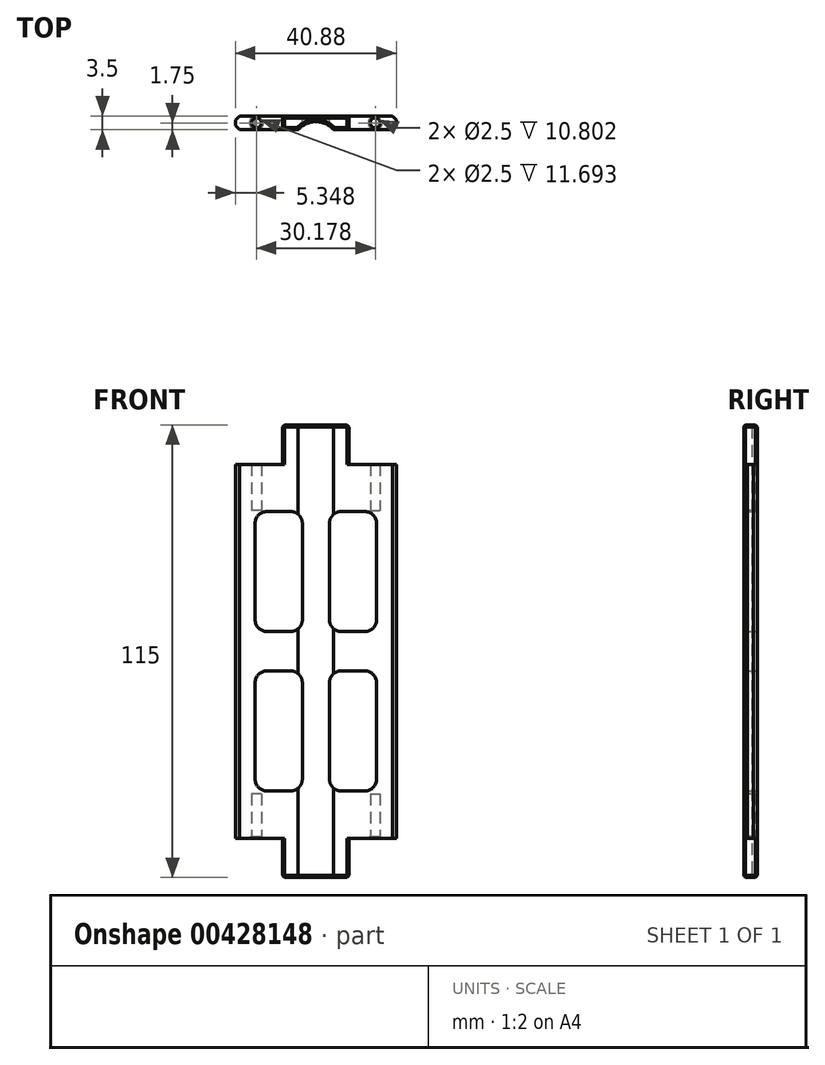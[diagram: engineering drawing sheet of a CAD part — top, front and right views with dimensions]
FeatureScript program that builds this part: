
annotation { "Feature Type Name" : "Feature", "Feature Type Description" : "" }
export const myFeature = defineFeature(function(context is Context, id is Id, definition is map)
    precondition{}
    {
        {
            var Q0;
            Q0=qCreatedBy(makeId("Top.planeOp"),FACE);
            var sketch = newSketch(context, id + "F0", { "sketchPlane" : qUnion([Q0])});
            skLineSegment(sketch, "E0", {"start": v(-26.48, 7.6) * mm, "end": v(-26.48, 21.4) * mm, "construction": true});
            skPoint(sketch, "E0.endSnap0", {"position": v(-26.48, 17.6) * mm});
            skLineSegment(sketch, "E1", {"start": v(-18.04, 15.1) * mm, "end": v(-18.04, 11.6) * mm});
            skLineSegment(sketch, "E2", {"start": v(-18.04, 11.6) * mm, "end": v(-21.94, 11.6) * mm});
            skLineSegment(sketch, "E3", {"start": v(-34.92, 11.6) * mm, "end": v(-34.92, 15.1) * mm});
            skLineSegment(sketch, "E4", {"start": v(-34.92, 15.1) * mm, "end": v(-18.04, 15.1) * mm});
            skArc(sketch, "E5", {"start": v(-21.94, 11.6) * mm, "mid": v(-26.48, 13.64) * mm, "end": v(-31.02, 11.6) * mm});
            skLineSegment(sketch, "E6.trimOffspring", {"start": v(-31.02, 11.6) * mm, "end": v(-34.92, 11.6) * mm});
            skLineSegment(sketch, "E7", {"start": v(-34.92, 13.34) * mm, "end": v(-1.9, 13.34) * mm, "construction": true});
            skLineSegment(sketch, "E8", {"start": v(-34.92, 13.34) * mm, "end": v(-48.22, 13.34) * mm, "construction": true});
            skCircle(sketch, "E9", {"center": v(-41.57, 13.34) * mm, "radius": 1.25 * mm});
            skCircle(sketch, "E10", {"center": v(-11.4, 13.34) * mm, "radius": 1.25 * mm});
            skSolve(sketch);
        }
        {
            var Q0;
            Q0=makeQuery(id+"F0.imprint","IMPRINT",FACE,{"disambiguationData":[TD([[makeQuery(id+"F0.imprint","IMPRINT",EDGE,{"derivedFrom":sQuery(id+"F0.wireOp",EDGE,"E1")}),-1.0]])]});
            extrude(context, id + "F1", {"entities" : qUnion([Q0]), "depth" : 115 * mm});
        }
        {
            var Q0;
            Q0=makeQuery(id+"F1.opExtrude","SWEPT_FACE",FACE,{"disambiguationData":[OSD([sQuery(id+"F0.wireOp",EDGE,"E1")])]});
            var sketch = newSketch(context, id + "F2", { "sketchPlane" : qUnion([Q0])});
            skLineSegment(sketch, "E11", {"start": v(11.6, 105) * mm, "end": v(15.1, 105) * mm});
            skLineSegment(sketch, "E12", {"start": v(15.1, 105) * mm, "end": v(15.1, 10) * mm});
            skLineSegment(sketch, "E13", {"start": v(15.1, 10) * mm, "end": v(11.6, 10) * mm});
            skLineSegment(sketch, "E14", {"start": v(11.6, 10) * mm, "end": v(11.6, 105) * mm});
            skSolve(sketch);
        }
        {
            var Q0;
            Q0=makeQuery(id+"F2.imprint","IMPRINT",FACE,{"disambiguationData":[TD([[makeQuery(id+"F2.imprint","IMPRINT",EDGE,{"derivedFrom":sQuery(id+"F2.wireOp",EDGE,"E11")}),-1.0]])]});
            extrude(context, id + "F3", {"entities" : qUnion([Q0]), "operationType" : NewBodyOperationType.ADD, "depth" : 12 * mm});
        }
        {
            var Q0;
            Q0=makeQuery(id+"F1.opExtrude","SWEPT_FACE",FACE,{"disambiguationData":[OSD([sQuery(id+"F0.wireOp",EDGE,"E3")])]});
            var sketch = newSketch(context, id + "F4", { "sketchPlane" : qUnion([Q0])});
            skLineSegment(sketch, "E15", {"start": v(-15.1, 105) * mm, "end": v(-11.6, 105) * mm});
            skLineSegment(sketch, "E16", {"start": v(-11.6, 105) * mm, "end": v(-11.6, 10) * mm});
            skLineSegment(sketch, "E17", {"start": v(-11.6, 10) * mm, "end": v(-15.1, 10) * mm});
            skLineSegment(sketch, "E18", {"start": v(-15.1, 10) * mm, "end": v(-15.1, 105) * mm});
            skSolve(sketch);
        }
        {
            var Q0;
            Q0=makeQuery(id+"F4.imprint","IMPRINT",FACE,{"disambiguationData":[TD([[makeQuery(id+"F4.imprint","IMPRINT",EDGE,{"derivedFrom":sQuery(id+"F4.wireOp",EDGE,"E15")}),-1.0]])]});
            extrude(context, id + "F5", {"entities" : qUnion([Q0]), "operationType" : NewBodyOperationType.ADD, "depth" : 12 * mm});
        }
        {
            var Q0;
            Q0=makeQuery(id+"F0.imprint","IMPRINT",FACE,{"disambiguationData":[TD([[makeQuery(id+"F0.imprint","IMPRINT",EDGE,{"derivedFrom":sQuery(id+"F0.wireOp",EDGE,"E9")}),1.0]])]});
            var Q1;
            Q1=makeQuery(id+"F0.imprint","IMPRINT",FACE,{"disambiguationData":[TD([[makeQuery(id+"F0.imprint","IMPRINT",EDGE,{"derivedFrom":sQuery(id+"F0.wireOp",EDGE,"E10")}),1.0]])]});
            var Q2;
            Q2=makeQuery(id+"F5.opExtrude","SWEPT_FACE",FACE,{"disambiguationData":[OSD([sQuery(id+"F4.wireOp",EDGE,"E15")])]});
            extrude(context, id + "F6", {"entities" : qUnion([Q0, Q1]), "operationType" : NewBodyOperationType.REMOVE, "endBound" : BoundingType.UP_TO_SURFACE, "endBoundEntityFace" : qUnion([Q2]), "depth" : 25 * mm});
        }
        {
            var Q0;
            Q0=makeQuery(id+"F5.boolean.opBoolean","MERGE",FACE,{"derivedFrom":[makeQuery(id+"F3.boolean.opBoolean","MERGE",FACE,{"derivedFrom":[makeQuery(id+"F1.opExtrude","SWEPT_FACE",FACE,{"disambiguationData":[OSD([sQuery(id+"F0.wireOp",EDGE,"E4")])]}),makeQuery(id+"F3.opExtrude","SWEPT_FACE",FACE,{"disambiguationData":[OSD([sQuery(id+"F2.wireOp",EDGE,"E12")])]})]}),makeQuery(id+"F5.opExtrude","SWEPT_FACE",FACE,{"disambiguationData":[OSD([sQuery(id+"F4.wireOp",EDGE,"E18")])]})]});
            var sketch = newSketch(context, id + "F7", { "sketchPlane" : qUnion([Q0])});
            skLineSegment(sketch, "E19.bottom", {"start": v(32.92, 93) * mm, "end": v(38.92, 93) * mm});
            skLineSegment(sketch, "E19.top", {"start": v(32.92, 62.5) * mm, "end": v(38.92, 62.5) * mm});
            skLineSegment(sketch, "E19.left", {"start": v(29.92, 90) * mm, "end": v(29.92, 65.5) * mm});
            skLineSegment(sketch, "E19.right", {"start": v(41.92, 90) * mm, "end": v(41.92, 65.5) * mm});
            skLineSegment(sketch, "E20", {"start": v(6.04, 105) * mm, "end": v(46.92, 105) * mm, "construction": true});
            skLineSegment(sketch, "E21", {"start": v(46.92, 105) * mm, "end": v(46.92, 10) * mm, "construction": true});
            skLineSegment(sketch, "E22", {"start": v(6.04, 57.5) * mm, "end": v(106.1, 57.5) * mm, "construction": true});
            skLineSegment(sketch, "E23", {"start": v(26.48, 105) * mm, "end": v(26.48, -23.84) * mm, "construction": true});
            skLineSegment(sketch, "E24.MirrorCS", {"start": v(20.04, 62.5) * mm, "end": v(14.04, 62.5) * mm});
            skLineSegment(sketch, "E25.MirrorCS", {"start": v(11.04, 90) * mm, "end": v(11.04, 65.5) * mm});
            skLineSegment(sketch, "E26.MirrorCS", {"start": v(20.04, 93) * mm, "end": v(14.04, 93) * mm});
            skLineSegment(sketch, "E27.MirrorCS", {"start": v(23.04, 90) * mm, "end": v(23.04, 65.5) * mm});
            skLineSegment(sketch, "E28.MirrorCS", {"start": v(20.04, 22) * mm, "end": v(14.04, 22) * mm});
            skLineSegment(sketch, "E29.MirrorCS", {"start": v(11.04, 25) * mm, "end": v(11.04, 49.5) * mm});
            skLineSegment(sketch, "E30.MirrorCS", {"start": v(20.04, 52.5) * mm, "end": v(14.04, 52.5) * mm});
            skLineSegment(sketch, "E31.MirrorCS", {"start": v(32.92, 52.5) * mm, "end": v(38.92, 52.5) * mm});
            skLineSegment(sketch, "E32.MirrorCS", {"start": v(32.92, 22) * mm, "end": v(38.92, 22) * mm});
            skLineSegment(sketch, "E33.MirrorCS", {"start": v(41.92, 25) * mm, "end": v(41.92, 49.5) * mm});
            skLineSegment(sketch, "E34.MirrorCS", {"start": v(29.92, 25) * mm, "end": v(29.92, 49.5) * mm});
            skLineSegment(sketch, "E35.MirrorCS", {"start": v(23.04, 25) * mm, "end": v(23.04, 49.5) * mm});
            skPoint(sketch, "E36.visualSharp", {"position": v(11.04, 93) * mm});
            skArc(sketch, "E36.filletArc", {"start": v(14.04, 93) * mm, "mid": v(11.92, 92.12) * mm, "end": v(11.04, 90) * mm});
            skPoint(sketch, "E37.visualSharp", {"position": v(23.04, 93) * mm});
            skArc(sketch, "E37.filletArc", {"start": v(23.04, 90) * mm, "mid": v(22.17, 92.12) * mm, "end": v(20.04, 93) * mm});
            skPoint(sketch, "E38.visualSharp", {"position": v(23.04, 62.5) * mm});
            skArc(sketch, "E38.filletArc", {"start": v(20.04, 62.5) * mm, "mid": v(22.17, 63.38) * mm, "end": v(23.04, 65.5) * mm});
            skPoint(sketch, "E39.visualSharp", {"position": v(11.04, 62.5) * mm});
            skArc(sketch, "E39.filletArc", {"start": v(11.04, 65.5) * mm, "mid": v(11.92, 63.38) * mm, "end": v(14.04, 62.5) * mm});
            skPoint(sketch, "E40.visualSharp", {"position": v(29.92, 93) * mm});
            skArc(sketch, "E40.filletArc", {"start": v(32.92, 93) * mm, "mid": v(30.8, 92.12) * mm, "end": v(29.92, 90) * mm});
            skPoint(sketch, "E41.visualSharp", {"position": v(41.92, 93) * mm});
            skArc(sketch, "E41.filletArc", {"start": v(41.92, 90) * mm, "mid": v(41.04, 92.12) * mm, "end": v(38.92, 93) * mm});
            skPoint(sketch, "E42.visualSharp", {"position": v(41.92, 62.5) * mm});
            skArc(sketch, "E42.filletArc", {"start": v(38.92, 62.5) * mm, "mid": v(41.04, 63.38) * mm, "end": v(41.92, 65.5) * mm});
            skPoint(sketch, "E43.visualSharp", {"position": v(29.92, 62.5) * mm});
            skArc(sketch, "E43.filletArc", {"start": v(29.92, 65.5) * mm, "mid": v(30.8, 63.38) * mm, "end": v(32.92, 62.5) * mm});
            skPoint(sketch, "E44.visualSharp", {"position": v(29.92, 52.5) * mm});
            skArc(sketch, "E44.filletArc", {"start": v(32.92, 52.5) * mm, "mid": v(30.8, 51.62) * mm, "end": v(29.92, 49.5) * mm});
            skPoint(sketch, "E45.visualSharp", {"position": v(41.92, 52.5) * mm});
            skArc(sketch, "E45.filletArc", {"start": v(41.92, 49.5) * mm, "mid": v(41.04, 51.62) * mm, "end": v(38.92, 52.5) * mm});
            skPoint(sketch, "E46.visualSharp", {"position": v(41.92, 22) * mm});
            skArc(sketch, "E46.filletArc", {"start": v(38.92, 22) * mm, "mid": v(41.04, 22.88) * mm, "end": v(41.92, 25) * mm});
            skPoint(sketch, "E47.visualSharp", {"position": v(29.92, 22) * mm});
            skArc(sketch, "E47.filletArc", {"start": v(29.92, 25) * mm, "mid": v(30.8, 22.88) * mm, "end": v(32.92, 22) * mm});
            skPoint(sketch, "E48.visualSharp", {"position": v(23.04, 52.5) * mm});
            skArc(sketch, "E48.filletArc", {"start": v(23.04, 49.5) * mm, "mid": v(22.17, 51.62) * mm, "end": v(20.04, 52.5) * mm});
            skPoint(sketch, "E49.visualSharp", {"position": v(11.04, 52.5) * mm});
            skArc(sketch, "E49.filletArc", {"start": v(14.04, 52.5) * mm, "mid": v(11.92, 51.62) * mm, "end": v(11.04, 49.5) * mm});
            skPoint(sketch, "E50.visualSharp", {"position": v(11.04, 22) * mm});
            skArc(sketch, "E50.filletArc", {"start": v(11.04, 25) * mm, "mid": v(11.92, 22.88) * mm, "end": v(14.04, 22) * mm});
            skPoint(sketch, "E51.visualSharp", {"position": v(23.04, 22) * mm});
            skArc(sketch, "E51.filletArc", {"start": v(20.04, 22) * mm, "mid": v(22.17, 22.88) * mm, "end": v(23.04, 25) * mm});
            skSolve(sketch);
        }
        {
            var Q0;
            Q0=makeQuery(id+"F7.imprint","IMPRINT",FACE,{"disambiguationData":[TD([[makeQuery(id+"F7.imprint","IMPRINT",EDGE,{"derivedFrom":sQuery(id+"F7.wireOp",EDGE,"E24.MirrorCS")}),-1.0]])]});
            var Q1;
            Q1=makeQuery(id+"F7.imprint","IMPRINT",FACE,{"disambiguationData":[TD([[makeQuery(id+"F7.imprint","IMPRINT",EDGE,{"derivedFrom":sQuery(id+"F7.wireOp",EDGE,"E19.bottom")}),-1.0]])]});
            var Q2;
            Q2=makeQuery(id+"F7.imprint","IMPRINT",FACE,{"disambiguationData":[TD([[makeQuery(id+"F7.imprint","IMPRINT",EDGE,{"derivedFrom":sQuery(id+"F7.wireOp",EDGE,"E28.MirrorCS")}),-1.0]])]});
            var Q3;
            Q3=makeQuery(id+"F7.imprint","IMPRINT",FACE,{"disambiguationData":[TD([[makeQuery(id+"F7.imprint","IMPRINT",EDGE,{"derivedFrom":sQuery(id+"F7.wireOp",EDGE,"E31.MirrorCS")}),-1.0]])]});
            var Q4;
            Q4=makeQuery(id+"F3.boolean.opBoolean","MERGE",FACE,{"derivedFrom":[makeQuery(id+"F1.opExtrude","SWEPT_FACE",FACE,{"disambiguationData":[OSD([sQuery(id+"F0.wireOp",EDGE,"E2")])]}),makeQuery(id+"F3.opExtrude","SWEPT_FACE",FACE,{"disambiguationData":[OSD([sQuery(id+"F2.wireOp",EDGE,"E14")])]})]});
            extrude(context, id + "F8", {"entities" : qUnion([Q0, Q1, Q2, Q3]), "operationType" : NewBodyOperationType.REMOVE, "endBound" : BoundingType.UP_TO_SURFACE, "oppositeDirection" : true, "endBoundEntityFace" : qUnion([Q4]), "depth" : 25 * mm});
        }
        {
            var Q0;
            Q0=makeQuery(id+"F5.boolean.opBoolean","MERGE",FACE,{"derivedFrom":[makeQuery(id+"F1.opExtrude","SWEPT_FACE",FACE,{"disambiguationData":[OSD([sQuery(id+"F0.wireOp",EDGE,"E6.trimOffspring")])]}),makeQuery(id+"F5.opExtrude","SWEPT_FACE",FACE,{"disambiguationData":[OSD([sQuery(id+"F4.wireOp",EDGE,"E16")])]})]});
            var sketch = newSketch(context, id + "F9", { "sketchPlane" : qUnion([Q0])});
            skLineSegment(sketch, "E52.bottom", {"start": v(-14.55, 93.3) * mm, "end": v(-8.57, 93.3) * mm});
            skLineSegment(sketch, "E52.top", {"start": v(-14.55, 21.3) * mm, "end": v(-8.57, 21.3) * mm});
            skLineSegment(sketch, "E52.right", {"start": v(-8.57, 93.3) * mm, "end": v(-8.57, 21.3) * mm});
            skLineSegment(sketch, "E53", {"start": v(-14.55, 93.3) * mm, "end": v(-14.55, 93) * mm});
            skLineSegment(sketch, "E54", {"start": v(-34.92, 115) * mm, "end": v(-17.69, 115) * mm, "construction": true});
            skLineSegment(sketch, "E55", {"start": v(-26.3, 115) * mm, "end": v(-26.3, -16.22) * mm, "construction": true});
            skLineSegment(sketch, "E56.MirrorCS", {"start": v(-38.06, 93.3) * mm, "end": v(-38.06, 21.3) * mm});
            skLineSegment(sketch, "E57.MirrorCS", {"start": v(-38.06, 21.3) * mm, "end": v(-44.05, 21.3) * mm});
            skLineSegment(sketch, "E58.MirrorCS", {"start": v(-44.05, 93.3) * mm, "end": v(-44.05, 21.3) * mm});
            skLineSegment(sketch, "E59.MirrorCS", {"start": v(-38.06, 93.3) * mm, "end": v(-44.05, 93.3) * mm});
            skLineSegment(sketch, "E60.0", {"start": v(-11.04, 90) * mm, "end": v(-11.04, 65.5) * mm});
            skArc(sketch, "E60.1", {"start": v(-14.04, 93) * mm, "mid": v(-11.92, 92.12) * mm, "end": v(-11.04, 90) * mm});
            skArc(sketch, "E60.2", {"start": v(-11.04, 65.5) * mm, "mid": v(-11.92, 63.38) * mm, "end": v(-14.04, 62.5) * mm});
            skLineSegment(sketch, "E60.3", {"start": v(-14.55, 62.5) * mm, "end": v(-14.04, 62.5) * mm});
            skLineSegment(sketch, "E60.4", {"start": v(-14.55, 93) * mm, "end": v(-14.04, 93) * mm});
            skPoint(sketch, "E61.orphan", {"position": v(-20.04, 93) * mm});
            skLineSegment(sketch, "E62.trimOffspring", {"start": v(-14.55, 62.5) * mm, "end": v(-14.55, 52.5) * mm});
            skPoint(sketch, "E63.orphan", {"position": v(-20.04, 62.5) * mm});
            skLineSegment(sketch, "E64.0", {"start": v(-14.55, 52.5) * mm, "end": v(-14.04, 52.5) * mm});
            skArc(sketch, "E64.1", {"start": v(-14.04, 52.5) * mm, "mid": v(-11.92, 51.62) * mm, "end": v(-11.04, 49.5) * mm});
            skLineSegment(sketch, "E64.2", {"start": v(-11.04, 25) * mm, "end": v(-11.04, 49.5) * mm});
            skLineSegment(sketch, "E64.3", {"start": v(-14.55, 22) * mm, "end": v(-14.04, 22) * mm});
            skArc(sketch, "E64.4", {"start": v(-11.04, 25) * mm, "mid": v(-11.92, 22.88) * mm, "end": v(-14.04, 22) * mm});
            skPoint(sketch, "E64.5", {"position": v(-11.04, 37.25) * mm});
            skPoint(sketch, "E65.orphan", {"position": v(-20.04, 52.5) * mm});
            skPoint(sketch, "E66.orphan", {"position": v(-20.04, 22) * mm});
            skLineSegment(sketch, "E67.trimOffspring", {"start": v(-14.55, 22) * mm, "end": v(-14.55, 21.3) * mm});
            skSolve(sketch);
        }
        {
            var Q0;
            {var subQ4=sQuery(id+"F9.wireOp",EDGE,"E57.MirrorCS");Q0=makeQuery(id+"F9.imprint","IMPRINT",FACE,{"disambiguationData":[TD([[makeQuery(id+"F9.imprint","IMPRINT",EDGE,{"derivedFrom":subQ4}),-1.0]])]});}
            var Q1;
            Q1=makeQuery(id+"F9.imprint","IMPRINT",FACE,{"disambiguationData":[TD([[makeQuery(id+"F9.imprint","IMPRINT",EDGE,{"derivedFrom":sQuery(id+"F9.wireOp",EDGE,"E52.bottom")}),-1.0]])]});
            var Q2;
            Q2=makeQuery(id+"F5.boolean.opBoolean","MERGE",FACE,{"derivedFrom":[makeQuery(id+"F3.boolean.opBoolean","MERGE",FACE,{"derivedFrom":[makeQuery(id+"F1.opExtrude","SWEPT_FACE",FACE,{"disambiguationData":[OSD([sQuery(id+"F0.wireOp",EDGE,"E4")])]}),makeQuery(id+"F3.opExtrude","SWEPT_FACE",FACE,{"disambiguationData":[OSD([sQuery(id+"F2.wireOp",EDGE,"E12")])]})]}),makeQuery(id+"F5.opExtrude","SWEPT_FACE",FACE,{"disambiguationData":[OSD([sQuery(id+"F4.wireOp",EDGE,"E18")])]})]});
            extrude(context, id + "F10", {"entities" : qUnion([Q0, Q1]), "operationType" : NewBodyOperationType.ADD, "endBound" : BoundingType.UP_TO_SURFACE, "oppositeDirection" : true, "endBoundEntityFace" : qUnion([Q2]), "depth" : 25 * mm});
        }
        {
            var Q0;
            Q0=makeQuery(id+"F8.boolean.opBoolean","COPY",EDGE,{"derivedFrom":makeQuery(id+"F8.opExtrude","TWEAK_EDGE",EDGE,{"derivedFrom":[makeQuery(id+"F3.boolean.opBoolean","MERGE",FACE,{"derivedFrom":[makeQuery(id+"F1.opExtrude","SWEPT_FACE",FACE,{"disambiguationData":[OSD([sQuery(id+"F0.wireOp",EDGE,"E2")])]}),makeQuery(id+"F3.opExtrude","SWEPT_FACE",FACE,{"disambiguationData":[OSD([sQuery(id+"F2.wireOp",EDGE,"E14")])]})]}),makeQuery(id+"F7.imprint","IMPRINT",EDGE,{"derivedFrom":sQuery(id+"F7.wireOp",EDGE,"E33.MirrorCS")})]})});
            var Q1;
            Q1=makeQuery(id+"F8.boolean.opBoolean","COPY",EDGE,{"derivedFrom":makeQuery(id+"F8.opExtrude","TWEAK_EDGE",EDGE,{"derivedFrom":[makeQuery(id+"F3.boolean.opBoolean","MERGE",FACE,{"derivedFrom":[makeQuery(id+"F1.opExtrude","SWEPT_FACE",FACE,{"disambiguationData":[OSD([sQuery(id+"F0.wireOp",EDGE,"E2")])]}),makeQuery(id+"F3.opExtrude","SWEPT_FACE",FACE,{"disambiguationData":[OSD([sQuery(id+"F2.wireOp",EDGE,"E14")])]})]}),makeQuery(id+"F7.imprint","IMPRINT",EDGE,{"derivedFrom":sQuery(id+"F7.wireOp",EDGE,"E45.filletArc")})]})});
            var Q2;
            Q2=makeQuery(id+"F8.boolean.opBoolean","COPY",EDGE,{"derivedFrom":makeQuery(id+"F8.opExtrude","TWEAK_EDGE",EDGE,{"derivedFrom":[makeQuery(id+"F3.boolean.opBoolean","MERGE",FACE,{"derivedFrom":[makeQuery(id+"F1.opExtrude","SWEPT_FACE",FACE,{"disambiguationData":[OSD([sQuery(id+"F0.wireOp",EDGE,"E2")])]}),makeQuery(id+"F3.opExtrude","SWEPT_FACE",FACE,{"disambiguationData":[OSD([sQuery(id+"F2.wireOp",EDGE,"E14")])]})]}),makeQuery(id+"F7.imprint","IMPRINT",EDGE,{"derivedFrom":sQuery(id+"F7.wireOp",EDGE,"E31.MirrorCS")})]})});
            var Q3;
            Q3=makeQuery(id+"F8.boolean.opBoolean","COPY",EDGE,{"derivedFrom":makeQuery(id+"F8.opExtrude","TWEAK_EDGE",EDGE,{"derivedFrom":[makeQuery(id+"F3.boolean.opBoolean","MERGE",FACE,{"derivedFrom":[makeQuery(id+"F1.opExtrude","SWEPT_FACE",FACE,{"disambiguationData":[OSD([sQuery(id+"F0.wireOp",EDGE,"E2")])]}),makeQuery(id+"F3.opExtrude","SWEPT_FACE",FACE,{"disambiguationData":[OSD([sQuery(id+"F2.wireOp",EDGE,"E14")])]})]}),makeQuery(id+"F7.imprint","IMPRINT",EDGE,{"derivedFrom":sQuery(id+"F7.wireOp",EDGE,"E44.filletArc")})]})});
            var Q4;
            Q4=makeQuery(id+"F8.boolean.opBoolean","COPY",EDGE,{"derivedFrom":makeQuery(id+"F8.opExtrude","TWEAK_EDGE",EDGE,{"derivedFrom":[makeQuery(id+"F3.boolean.opBoolean","MERGE",FACE,{"derivedFrom":[makeQuery(id+"F1.opExtrude","SWEPT_FACE",FACE,{"disambiguationData":[OSD([sQuery(id+"F0.wireOp",EDGE,"E2")])]}),makeQuery(id+"F3.opExtrude","SWEPT_FACE",FACE,{"disambiguationData":[OSD([sQuery(id+"F2.wireOp",EDGE,"E14")])]})]}),makeQuery(id+"F7.imprint","IMPRINT",EDGE,{"derivedFrom":sQuery(id+"F7.wireOp",EDGE,"E47.filletArc")})]})});
            var Q5;
            Q5=makeQuery(id+"F8.boolean.opBoolean","COPY",EDGE,{"derivedFrom":makeQuery(id+"F8.opExtrude","TWEAK_EDGE",EDGE,{"derivedFrom":[makeQuery(id+"F3.boolean.opBoolean","MERGE",FACE,{"derivedFrom":[makeQuery(id+"F1.opExtrude","SWEPT_FACE",FACE,{"disambiguationData":[OSD([sQuery(id+"F0.wireOp",EDGE,"E2")])]}),makeQuery(id+"F3.opExtrude","SWEPT_FACE",FACE,{"disambiguationData":[OSD([sQuery(id+"F2.wireOp",EDGE,"E14")])]})]}),makeQuery(id+"F7.imprint","IMPRINT",EDGE,{"derivedFrom":sQuery(id+"F7.wireOp",EDGE,"E32.MirrorCS")})]})});
            var Q6;
            Q6=makeQuery(id+"F8.boolean.opBoolean","COPY",EDGE,{"derivedFrom":makeQuery(id+"F8.opExtrude","TWEAK_EDGE",EDGE,{"derivedFrom":[makeQuery(id+"F3.boolean.opBoolean","MERGE",FACE,{"derivedFrom":[makeQuery(id+"F1.opExtrude","SWEPT_FACE",FACE,{"disambiguationData":[OSD([sQuery(id+"F0.wireOp",EDGE,"E2")])]}),makeQuery(id+"F3.opExtrude","SWEPT_FACE",FACE,{"disambiguationData":[OSD([sQuery(id+"F2.wireOp",EDGE,"E14")])]})]}),makeQuery(id+"F7.imprint","IMPRINT",EDGE,{"derivedFrom":sQuery(id+"F7.wireOp",EDGE,"E46.filletArc")})]})});
            var Q7;
            Q7=makeQuery(id+"F8.boolean.opBoolean","COPY",EDGE,{"derivedFrom":makeQuery(id+"F8.opExtrude","CAP_EDGE",EDGE,{"disambiguationData":[OSD([sQuery(id+"F7.wireOp",EDGE,"E33.MirrorCS")])],"isStart":true})});
            var Q8;
            Q8=makeQuery(id+"F8.boolean.opBoolean","COPY",EDGE,{"derivedFrom":makeQuery(id+"F8.opExtrude","CAP_EDGE",EDGE,{"disambiguationData":[OSD([sQuery(id+"F7.wireOp",EDGE,"E45.filletArc")])],"isStart":true})});
            var Q9;
            Q9=makeQuery(id+"F8.boolean.opBoolean","COPY",EDGE,{"derivedFrom":makeQuery(id+"F8.opExtrude","CAP_EDGE",EDGE,{"disambiguationData":[OSD([sQuery(id+"F7.wireOp",EDGE,"E31.MirrorCS")])],"isStart":true})});
            var Q10;
            Q10=makeQuery(id+"F8.boolean.opBoolean","COPY",EDGE,{"derivedFrom":makeQuery(id+"F8.opExtrude","CAP_EDGE",EDGE,{"disambiguationData":[OSD([sQuery(id+"F7.wireOp",EDGE,"E44.filletArc")])],"isStart":true})});
            var Q11;
            Q11=makeQuery(id+"F8.boolean.opBoolean","COPY",EDGE,{"derivedFrom":makeQuery(id+"F8.opExtrude","TWEAK_EDGE",EDGE,{"derivedFrom":[makeQuery(id+"F3.boolean.opBoolean","MERGE",FACE,{"derivedFrom":[makeQuery(id+"F1.opExtrude","SWEPT_FACE",FACE,{"disambiguationData":[OSD([sQuery(id+"F0.wireOp",EDGE,"E2")])]}),makeQuery(id+"F3.opExtrude","SWEPT_FACE",FACE,{"disambiguationData":[OSD([sQuery(id+"F2.wireOp",EDGE,"E14")])]})]}),makeQuery(id+"F7.imprint","IMPRINT",EDGE,{"derivedFrom":sQuery(id+"F7.wireOp",EDGE,"E30.MirrorCS")})]})});
            var Q12;
            Q12=makeQuery(id+"F8.boolean.opBoolean","COPY",EDGE,{"derivedFrom":makeQuery(id+"F8.opExtrude","TWEAK_EDGE",EDGE,{"derivedFrom":[makeQuery(id+"F3.boolean.opBoolean","MERGE",FACE,{"derivedFrom":[makeQuery(id+"F1.opExtrude","SWEPT_FACE",FACE,{"disambiguationData":[OSD([sQuery(id+"F0.wireOp",EDGE,"E2")])]}),makeQuery(id+"F3.opExtrude","SWEPT_FACE",FACE,{"disambiguationData":[OSD([sQuery(id+"F2.wireOp",EDGE,"E14")])]})]}),makeQuery(id+"F7.imprint","IMPRINT",EDGE,{"derivedFrom":sQuery(id+"F7.wireOp",EDGE,"E48.filletArc")})]})});
            var Q13;
            Q13=makeQuery(id+"F8.boolean.opBoolean","COPY",EDGE,{"derivedFrom":makeQuery(id+"F8.opExtrude","TWEAK_EDGE",EDGE,{"derivedFrom":[makeQuery(id+"F3.boolean.opBoolean","MERGE",FACE,{"derivedFrom":[makeQuery(id+"F1.opExtrude","SWEPT_FACE",FACE,{"disambiguationData":[OSD([sQuery(id+"F0.wireOp",EDGE,"E2")])]}),makeQuery(id+"F3.opExtrude","SWEPT_FACE",FACE,{"disambiguationData":[OSD([sQuery(id+"F2.wireOp",EDGE,"E14")])]})]}),makeQuery(id+"F7.imprint","IMPRINT",EDGE,{"derivedFrom":sQuery(id+"F7.wireOp",EDGE,"E51.filletArc")})]})});
            var Q14;
            Q14=makeQuery(id+"F8.boolean.opBoolean","COPY",EDGE,{"derivedFrom":makeQuery(id+"F8.opExtrude","TWEAK_EDGE",EDGE,{"derivedFrom":[makeQuery(id+"F3.boolean.opBoolean","MERGE",FACE,{"derivedFrom":[makeQuery(id+"F1.opExtrude","SWEPT_FACE",FACE,{"disambiguationData":[OSD([sQuery(id+"F0.wireOp",EDGE,"E2")])]}),makeQuery(id+"F3.opExtrude","SWEPT_FACE",FACE,{"disambiguationData":[OSD([sQuery(id+"F2.wireOp",EDGE,"E14")])]})]}),makeQuery(id+"F7.imprint","IMPRINT",EDGE,{"derivedFrom":sQuery(id+"F7.wireOp",EDGE,"E28.MirrorCS")})]})});
            var Q15;
            Q15=makeQuery(id+"F8.boolean.opBoolean","COPY",EDGE,{"derivedFrom":makeQuery(id+"F8.opExtrude","TWEAK_EDGE",EDGE,{"derivedFrom":[makeQuery(id+"F3.boolean.opBoolean","MERGE",FACE,{"derivedFrom":[makeQuery(id+"F1.opExtrude","SWEPT_FACE",FACE,{"disambiguationData":[OSD([sQuery(id+"F0.wireOp",EDGE,"E2")])]}),makeQuery(id+"F3.opExtrude","SWEPT_FACE",FACE,{"disambiguationData":[OSD([sQuery(id+"F2.wireOp",EDGE,"E14")])]})]}),makeQuery(id+"F7.imprint","IMPRINT",EDGE,{"derivedFrom":sQuery(id+"F7.wireOp",EDGE,"E50.filletArc")})]})});
            var Q16;
            Q16=makeQuery(id+"F8.boolean.opBoolean","COPY",EDGE,{"derivedFrom":makeQuery(id+"F8.opExtrude","TWEAK_EDGE",EDGE,{"derivedFrom":[makeQuery(id+"F3.boolean.opBoolean","MERGE",FACE,{"derivedFrom":[makeQuery(id+"F1.opExtrude","SWEPT_FACE",FACE,{"disambiguationData":[OSD([sQuery(id+"F0.wireOp",EDGE,"E2")])]}),makeQuery(id+"F3.opExtrude","SWEPT_FACE",FACE,{"disambiguationData":[OSD([sQuery(id+"F2.wireOp",EDGE,"E14")])]})]}),makeQuery(id+"F7.imprint","IMPRINT",EDGE,{"derivedFrom":sQuery(id+"F7.wireOp",EDGE,"E29.MirrorCS")})]})});
            var Q17;
            Q17=makeQuery(id+"F8.boolean.opBoolean","COPY",EDGE,{"derivedFrom":makeQuery(id+"F8.opExtrude","TWEAK_EDGE",EDGE,{"derivedFrom":[makeQuery(id+"F3.boolean.opBoolean","MERGE",FACE,{"derivedFrom":[makeQuery(id+"F1.opExtrude","SWEPT_FACE",FACE,{"disambiguationData":[OSD([sQuery(id+"F0.wireOp",EDGE,"E2")])]}),makeQuery(id+"F3.opExtrude","SWEPT_FACE",FACE,{"disambiguationData":[OSD([sQuery(id+"F2.wireOp",EDGE,"E14")])]})]}),makeQuery(id+"F7.imprint","IMPRINT",EDGE,{"derivedFrom":sQuery(id+"F7.wireOp",EDGE,"E49.filletArc")})]})});
            var Q18;
            Q18=makeQuery(id+"F8.boolean.opBoolean","COPY",EDGE,{"derivedFrom":makeQuery(id+"F8.opExtrude","CAP_EDGE",EDGE,{"disambiguationData":[OSD([sQuery(id+"F7.wireOp",EDGE,"E35.MirrorCS")])],"isStart":true})});
            var Q19;
            Q19=makeQuery(id+"F8.boolean.opBoolean","COPY",EDGE,{"derivedFrom":makeQuery(id+"F8.opExtrude","CAP_EDGE",EDGE,{"disambiguationData":[OSD([sQuery(id+"F7.wireOp",EDGE,"E48.filletArc")])],"isStart":true})});
            var Q20;
            Q20=makeQuery(id+"F8.boolean.opBoolean","COPY",EDGE,{"derivedFrom":makeQuery(id+"F8.opExtrude","CAP_EDGE",EDGE,{"disambiguationData":[OSD([sQuery(id+"F7.wireOp",EDGE,"E30.MirrorCS")])],"isStart":true})});
            var Q21;
            Q21=makeQuery(id+"F8.boolean.opBoolean","COPY",EDGE,{"derivedFrom":makeQuery(id+"F8.opExtrude","CAP_EDGE",EDGE,{"disambiguationData":[OSD([sQuery(id+"F7.wireOp",EDGE,"E46.filletArc")])],"isStart":true})});
            var Q22;
            Q22=makeQuery(id+"F8.boolean.opBoolean","COPY",EDGE,{"derivedFrom":makeQuery(id+"F8.opExtrude","CAP_EDGE",EDGE,{"disambiguationData":[OSD([sQuery(id+"F7.wireOp",EDGE,"E32.MirrorCS")])],"isStart":true})});
            var Q23;
            Q23=makeQuery(id+"F8.boolean.opBoolean","COPY",EDGE,{"derivedFrom":makeQuery(id+"F8.opExtrude","CAP_EDGE",EDGE,{"disambiguationData":[OSD([sQuery(id+"F7.wireOp",EDGE,"E47.filletArc")])],"isStart":true})});
            var Q24;
            Q24=makeQuery(id+"F8.boolean.opBoolean","COPY",EDGE,{"derivedFrom":makeQuery(id+"F8.opExtrude","CAP_EDGE",EDGE,{"disambiguationData":[OSD([sQuery(id+"F7.wireOp",EDGE,"E51.filletArc")])],"isStart":true})});
            var Q25;
            Q25=makeQuery(id+"F8.boolean.opBoolean","COPY",EDGE,{"derivedFrom":makeQuery(id+"F8.opExtrude","CAP_EDGE",EDGE,{"disambiguationData":[OSD([sQuery(id+"F7.wireOp",EDGE,"E28.MirrorCS")])],"isStart":true})});
            var Q26;
            Q26=makeQuery(id+"F8.boolean.opBoolean","COPY",EDGE,{"derivedFrom":makeQuery(id+"F8.opExtrude","CAP_EDGE",EDGE,{"disambiguationData":[OSD([sQuery(id+"F7.wireOp",EDGE,"E50.filletArc")])],"isStart":true})});
            var Q27;
            Q27=makeQuery(id+"F8.boolean.opBoolean","COPY",EDGE,{"derivedFrom":makeQuery(id+"F8.opExtrude","CAP_EDGE",EDGE,{"disambiguationData":[OSD([sQuery(id+"F7.wireOp",EDGE,"E29.MirrorCS")])],"isStart":true})});
            var Q28;
            Q28=makeQuery(id+"F8.boolean.opBoolean","COPY",EDGE,{"derivedFrom":makeQuery(id+"F8.opExtrude","CAP_EDGE",EDGE,{"disambiguationData":[OSD([sQuery(id+"F7.wireOp",EDGE,"E49.filletArc")])],"isStart":true})});
            var Q29;
            Q29=makeQuery(id+"F8.boolean.opBoolean","COPY",EDGE,{"derivedFrom":makeQuery(id+"F8.opExtrude","CAP_EDGE",EDGE,{"disambiguationData":[OSD([sQuery(id+"F7.wireOp",EDGE,"E43.filletArc")])],"isStart":true})});
            var Q30;
            Q30=makeQuery(id+"F8.boolean.opBoolean","COPY",EDGE,{"derivedFrom":makeQuery(id+"F8.opExtrude","TWEAK_EDGE",EDGE,{"derivedFrom":[makeQuery(id+"F3.boolean.opBoolean","MERGE",FACE,{"derivedFrom":[makeQuery(id+"F1.opExtrude","SWEPT_FACE",FACE,{"disambiguationData":[OSD([sQuery(id+"F0.wireOp",EDGE,"E2")])]}),makeQuery(id+"F3.opExtrude","SWEPT_FACE",FACE,{"disambiguationData":[OSD([sQuery(id+"F2.wireOp",EDGE,"E14")])]})]}),makeQuery(id+"F7.imprint","IMPRINT",EDGE,{"derivedFrom":sQuery(id+"F7.wireOp",EDGE,"E43.filletArc")})]})});
            var Q31;
            Q31=makeQuery(id+"F8.boolean.opBoolean","COPY",EDGE,{"derivedFrom":makeQuery(id+"F8.opExtrude","TWEAK_EDGE",EDGE,{"derivedFrom":[makeQuery(id+"F3.boolean.opBoolean","MERGE",FACE,{"derivedFrom":[makeQuery(id+"F1.opExtrude","SWEPT_FACE",FACE,{"disambiguationData":[OSD([sQuery(id+"F0.wireOp",EDGE,"E2")])]}),makeQuery(id+"F3.opExtrude","SWEPT_FACE",FACE,{"disambiguationData":[OSD([sQuery(id+"F2.wireOp",EDGE,"E14")])]})]}),makeQuery(id+"F7.imprint","IMPRINT",EDGE,{"derivedFrom":sQuery(id+"F7.wireOp",EDGE,"E19.top")})]})});
            var Q32;
            Q32=makeQuery(id+"F8.boolean.opBoolean","COPY",EDGE,{"derivedFrom":makeQuery(id+"F8.opExtrude","CAP_EDGE",EDGE,{"disambiguationData":[OSD([sQuery(id+"F7.wireOp",EDGE,"E19.top")])],"isStart":true})});
            var Q33;
            Q33=makeQuery(id+"F8.boolean.opBoolean","COPY",EDGE,{"derivedFrom":makeQuery(id+"F8.opExtrude","TWEAK_EDGE",EDGE,{"derivedFrom":[makeQuery(id+"F3.boolean.opBoolean","MERGE",FACE,{"derivedFrom":[makeQuery(id+"F1.opExtrude","SWEPT_FACE",FACE,{"disambiguationData":[OSD([sQuery(id+"F0.wireOp",EDGE,"E2")])]}),makeQuery(id+"F3.opExtrude","SWEPT_FACE",FACE,{"disambiguationData":[OSD([sQuery(id+"F2.wireOp",EDGE,"E14")])]})]}),makeQuery(id+"F7.imprint","IMPRINT",EDGE,{"derivedFrom":sQuery(id+"F7.wireOp",EDGE,"E42.filletArc")})]})});
            var Q34;
            Q34=makeQuery(id+"F8.boolean.opBoolean","COPY",EDGE,{"derivedFrom":makeQuery(id+"F8.opExtrude","CAP_EDGE",EDGE,{"disambiguationData":[OSD([sQuery(id+"F7.wireOp",EDGE,"E42.filletArc")])],"isStart":true})});
            var Q35;
            Q35=makeQuery(id+"F8.boolean.opBoolean","COPY",EDGE,{"derivedFrom":makeQuery(id+"F8.opExtrude","CAP_EDGE",EDGE,{"disambiguationData":[OSD([sQuery(id+"F7.wireOp",EDGE,"E19.left")])],"isStart":true})});
            var Q36;
            Q36=makeQuery(id+"F8.boolean.opBoolean","COPY",EDGE,{"derivedFrom":makeQuery(id+"F8.opExtrude","CAP_EDGE",EDGE,{"disambiguationData":[OSD([sQuery(id+"F7.wireOp",EDGE,"E24.MirrorCS")])],"isStart":true})});
            var Q37;
            Q37=makeQuery(id+"F8.boolean.opBoolean","COPY",EDGE,{"derivedFrom":makeQuery(id+"F8.opExtrude","CAP_EDGE",EDGE,{"disambiguationData":[OSD([sQuery(id+"F7.wireOp",EDGE,"E39.filletArc")])],"isStart":true})});
            var Q38;
            Q38=makeQuery(id+"F8.boolean.opBoolean","COPY",EDGE,{"derivedFrom":makeQuery(id+"F8.opExtrude","TWEAK_EDGE",EDGE,{"derivedFrom":[makeQuery(id+"F3.boolean.opBoolean","MERGE",FACE,{"derivedFrom":[makeQuery(id+"F1.opExtrude","SWEPT_FACE",FACE,{"disambiguationData":[OSD([sQuery(id+"F0.wireOp",EDGE,"E2")])]}),makeQuery(id+"F3.opExtrude","SWEPT_FACE",FACE,{"disambiguationData":[OSD([sQuery(id+"F2.wireOp",EDGE,"E14")])]})]}),makeQuery(id+"F7.imprint","IMPRINT",EDGE,{"derivedFrom":sQuery(id+"F7.wireOp",EDGE,"E39.filletArc")})]})});
            var Q39;
            Q39=makeQuery(id+"F8.boolean.opBoolean","COPY",EDGE,{"derivedFrom":makeQuery(id+"F8.opExtrude","TWEAK_EDGE",EDGE,{"derivedFrom":[makeQuery(id+"F3.boolean.opBoolean","MERGE",FACE,{"derivedFrom":[makeQuery(id+"F1.opExtrude","SWEPT_FACE",FACE,{"disambiguationData":[OSD([sQuery(id+"F0.wireOp",EDGE,"E2")])]}),makeQuery(id+"F3.opExtrude","SWEPT_FACE",FACE,{"disambiguationData":[OSD([sQuery(id+"F2.wireOp",EDGE,"E14")])]})]}),makeQuery(id+"F7.imprint","IMPRINT",EDGE,{"derivedFrom":sQuery(id+"F7.wireOp",EDGE,"E24.MirrorCS")})]})});
            var Q40;
            Q40=makeQuery(id+"F8.boolean.opBoolean","COPY",EDGE,{"derivedFrom":makeQuery(id+"F8.opExtrude","TWEAK_EDGE",EDGE,{"derivedFrom":[makeQuery(id+"F3.boolean.opBoolean","MERGE",FACE,{"derivedFrom":[makeQuery(id+"F1.opExtrude","SWEPT_FACE",FACE,{"disambiguationData":[OSD([sQuery(id+"F0.wireOp",EDGE,"E2")])]}),makeQuery(id+"F3.opExtrude","SWEPT_FACE",FACE,{"disambiguationData":[OSD([sQuery(id+"F2.wireOp",EDGE,"E14")])]})]}),makeQuery(id+"F7.imprint","IMPRINT",EDGE,{"derivedFrom":sQuery(id+"F7.wireOp",EDGE,"E38.filletArc")})]})});
            var Q41;
            Q41=makeQuery(id+"F8.boolean.opBoolean","COPY",EDGE,{"derivedFrom":makeQuery(id+"F8.opExtrude","TWEAK_EDGE",EDGE,{"derivedFrom":[makeQuery(id+"F3.boolean.opBoolean","MERGE",FACE,{"derivedFrom":[makeQuery(id+"F1.opExtrude","SWEPT_FACE",FACE,{"disambiguationData":[OSD([sQuery(id+"F0.wireOp",EDGE,"E2")])]}),makeQuery(id+"F3.opExtrude","SWEPT_FACE",FACE,{"disambiguationData":[OSD([sQuery(id+"F2.wireOp",EDGE,"E14")])]})]}),makeQuery(id+"F7.imprint","IMPRINT",EDGE,{"derivedFrom":sQuery(id+"F7.wireOp",EDGE,"E25.MirrorCS")})]})});
            var Q42;
            Q42=makeQuery(id+"F8.boolean.opBoolean","COPY",EDGE,{"derivedFrom":makeQuery(id+"F8.opExtrude","TWEAK_EDGE",EDGE,{"derivedFrom":[makeQuery(id+"F3.boolean.opBoolean","MERGE",FACE,{"derivedFrom":[makeQuery(id+"F1.opExtrude","SWEPT_FACE",FACE,{"disambiguationData":[OSD([sQuery(id+"F0.wireOp",EDGE,"E2")])]}),makeQuery(id+"F3.opExtrude","SWEPT_FACE",FACE,{"disambiguationData":[OSD([sQuery(id+"F2.wireOp",EDGE,"E14")])]})]}),makeQuery(id+"F7.imprint","IMPRINT",EDGE,{"derivedFrom":sQuery(id+"F7.wireOp",EDGE,"E36.filletArc")})]})});
            var Q43;
            Q43=makeQuery(id+"F8.boolean.opBoolean","COPY",EDGE,{"derivedFrom":makeQuery(id+"F8.opExtrude","TWEAK_EDGE",EDGE,{"derivedFrom":[makeQuery(id+"F3.boolean.opBoolean","MERGE",FACE,{"derivedFrom":[makeQuery(id+"F1.opExtrude","SWEPT_FACE",FACE,{"disambiguationData":[OSD([sQuery(id+"F0.wireOp",EDGE,"E2")])]}),makeQuery(id+"F3.opExtrude","SWEPT_FACE",FACE,{"disambiguationData":[OSD([sQuery(id+"F2.wireOp",EDGE,"E14")])]})]}),makeQuery(id+"F7.imprint","IMPRINT",EDGE,{"derivedFrom":sQuery(id+"F7.wireOp",EDGE,"E26.MirrorCS")})]})});
            var Q44;
            Q44=makeQuery(id+"F8.boolean.opBoolean","COPY",EDGE,{"derivedFrom":makeQuery(id+"F8.opExtrude","TWEAK_EDGE",EDGE,{"derivedFrom":[makeQuery(id+"F3.boolean.opBoolean","MERGE",FACE,{"derivedFrom":[makeQuery(id+"F1.opExtrude","SWEPT_FACE",FACE,{"disambiguationData":[OSD([sQuery(id+"F0.wireOp",EDGE,"E2")])]}),makeQuery(id+"F3.opExtrude","SWEPT_FACE",FACE,{"disambiguationData":[OSD([sQuery(id+"F2.wireOp",EDGE,"E14")])]})]}),makeQuery(id+"F7.imprint","IMPRINT",EDGE,{"derivedFrom":sQuery(id+"F7.wireOp",EDGE,"E37.filletArc")})]})});
            var Q45;
            Q45=makeQuery(id+"F8.boolean.opBoolean","COPY",EDGE,{"derivedFrom":makeQuery(id+"F8.opExtrude","CAP_EDGE",EDGE,{"disambiguationData":[OSD([sQuery(id+"F7.wireOp",EDGE,"E25.MirrorCS")])],"isStart":true})});
            var Q46;
            Q46=makeQuery(id+"F8.boolean.opBoolean","COPY",EDGE,{"derivedFrom":makeQuery(id+"F8.opExtrude","CAP_EDGE",EDGE,{"disambiguationData":[OSD([sQuery(id+"F7.wireOp",EDGE,"E38.filletArc")])],"isStart":true})});
            var Q47;
            Q47=makeQuery(id+"F8.boolean.opBoolean","COPY",EDGE,{"derivedFrom":makeQuery(id+"F8.opExtrude","CAP_EDGE",EDGE,{"disambiguationData":[OSD([sQuery(id+"F7.wireOp",EDGE,"E27.MirrorCS")])],"isStart":true})});
            var Q48;
            Q48=makeQuery(id+"F8.boolean.opBoolean","COPY",EDGE,{"derivedFrom":makeQuery(id+"F8.opExtrude","CAP_EDGE",EDGE,{"disambiguationData":[OSD([sQuery(id+"F7.wireOp",EDGE,"E36.filletArc")])],"isStart":true})});
            var Q49;
            Q49=makeQuery(id+"F8.boolean.opBoolean","COPY",EDGE,{"derivedFrom":makeQuery(id+"F8.opExtrude","CAP_EDGE",EDGE,{"disambiguationData":[OSD([sQuery(id+"F7.wireOp",EDGE,"E26.MirrorCS")])],"isStart":true})});
            var Q50;
            Q50=makeQuery(id+"F8.boolean.opBoolean","COPY",EDGE,{"derivedFrom":makeQuery(id+"F8.opExtrude","CAP_EDGE",EDGE,{"disambiguationData":[OSD([sQuery(id+"F7.wireOp",EDGE,"E37.filletArc")])],"isStart":true})});
            var Q51;
            Q51=makeQuery(id+"F8.boolean.opBoolean","COPY",EDGE,{"derivedFrom":makeQuery(id+"F8.opExtrude","CAP_EDGE",EDGE,{"disambiguationData":[OSD([sQuery(id+"F7.wireOp",EDGE,"E19.right")])],"isStart":true})});
            var Q52;
            Q52=makeQuery(id+"F8.boolean.opBoolean","COPY",EDGE,{"derivedFrom":makeQuery(id+"F8.opExtrude","TWEAK_EDGE",EDGE,{"derivedFrom":[makeQuery(id+"F3.boolean.opBoolean","MERGE",FACE,{"derivedFrom":[makeQuery(id+"F1.opExtrude","SWEPT_FACE",FACE,{"disambiguationData":[OSD([sQuery(id+"F0.wireOp",EDGE,"E2")])]}),makeQuery(id+"F3.opExtrude","SWEPT_FACE",FACE,{"disambiguationData":[OSD([sQuery(id+"F2.wireOp",EDGE,"E14")])]})]}),makeQuery(id+"F7.imprint","IMPRINT",EDGE,{"derivedFrom":sQuery(id+"F7.wireOp",EDGE,"E19.right")})]})});
            var Q53;
            Q53=makeQuery(id+"F8.boolean.opBoolean","COPY",EDGE,{"derivedFrom":makeQuery(id+"F8.opExtrude","TWEAK_EDGE",EDGE,{"derivedFrom":[makeQuery(id+"F3.boolean.opBoolean","MERGE",FACE,{"derivedFrom":[makeQuery(id+"F1.opExtrude","SWEPT_FACE",FACE,{"disambiguationData":[OSD([sQuery(id+"F0.wireOp",EDGE,"E2")])]}),makeQuery(id+"F3.opExtrude","SWEPT_FACE",FACE,{"disambiguationData":[OSD([sQuery(id+"F2.wireOp",EDGE,"E14")])]})]}),makeQuery(id+"F7.imprint","IMPRINT",EDGE,{"derivedFrom":sQuery(id+"F7.wireOp",EDGE,"E41.filletArc")})]})});
            var Q54;
            Q54=makeQuery(id+"F8.boolean.opBoolean","COPY",EDGE,{"derivedFrom":makeQuery(id+"F8.opExtrude","CAP_EDGE",EDGE,{"disambiguationData":[OSD([sQuery(id+"F7.wireOp",EDGE,"E41.filletArc")])],"isStart":true})});
            var Q55;
            Q55=makeQuery(id+"F8.boolean.opBoolean","COPY",EDGE,{"derivedFrom":makeQuery(id+"F8.opExtrude","TWEAK_EDGE",EDGE,{"derivedFrom":[makeQuery(id+"F3.boolean.opBoolean","MERGE",FACE,{"derivedFrom":[makeQuery(id+"F1.opExtrude","SWEPT_FACE",FACE,{"disambiguationData":[OSD([sQuery(id+"F0.wireOp",EDGE,"E2")])]}),makeQuery(id+"F3.opExtrude","SWEPT_FACE",FACE,{"disambiguationData":[OSD([sQuery(id+"F2.wireOp",EDGE,"E14")])]})]}),makeQuery(id+"F7.imprint","IMPRINT",EDGE,{"derivedFrom":sQuery(id+"F7.wireOp",EDGE,"E19.bottom")})]})});
            var Q56;
            Q56=makeQuery(id+"F8.boolean.opBoolean","COPY",EDGE,{"derivedFrom":makeQuery(id+"F8.opExtrude","CAP_EDGE",EDGE,{"disambiguationData":[OSD([sQuery(id+"F7.wireOp",EDGE,"E19.bottom")])],"isStart":true})});
            var Q57;
            Q57=makeQuery(id+"F8.boolean.opBoolean","COPY",EDGE,{"derivedFrom":makeQuery(id+"F8.opExtrude","TWEAK_EDGE",EDGE,{"derivedFrom":[makeQuery(id+"F3.boolean.opBoolean","MERGE",FACE,{"derivedFrom":[makeQuery(id+"F1.opExtrude","SWEPT_FACE",FACE,{"disambiguationData":[OSD([sQuery(id+"F0.wireOp",EDGE,"E2")])]}),makeQuery(id+"F3.opExtrude","SWEPT_FACE",FACE,{"disambiguationData":[OSD([sQuery(id+"F2.wireOp",EDGE,"E14")])]})]}),makeQuery(id+"F7.imprint","IMPRINT",EDGE,{"derivedFrom":sQuery(id+"F7.wireOp",EDGE,"E40.filletArc")})]})});
            var Q58;
            Q58=makeQuery(id+"F8.boolean.opBoolean","COPY",EDGE,{"derivedFrom":makeQuery(id+"F8.opExtrude","CAP_EDGE",EDGE,{"disambiguationData":[OSD([sQuery(id+"F7.wireOp",EDGE,"E40.filletArc")])],"isStart":true})});
            var Q59;
            Q59=makeQuery(id+"F3.opExtrude","CAP_EDGE",EDGE,{"disambiguationData":[OSD([sQuery(id+"F2.wireOp",EDGE,"E14")])],"isStart":false});
            var Q60;
            Q60=makeQuery(id+"F3.opExtrude","CAP_EDGE",EDGE,{"disambiguationData":[OSD([sQuery(id+"F2.wireOp",EDGE,"E12")])],"isStart":false});
            var Q61;
            Q61=makeQuery(id+"F5.opExtrude","CAP_EDGE",EDGE,{"disambiguationData":[OSD([sQuery(id+"F4.wireOp",EDGE,"E16")])],"isStart":false});
            var Q62;
            Q62=makeQuery(id+"F5.opExtrude","CAP_EDGE",EDGE,{"disambiguationData":[OSD([sQuery(id+"F4.wireOp",EDGE,"E18")])],"isStart":false});
            chamfer(context, id + "F11", {"entities" : qUnion([Q0, Q1, Q2, Q3, Q4, Q5, Q6, Q7, Q8, Q9, Q10, Q11, Q12, Q13, Q14, Q15, Q16, Q17, Q18, Q19, Q20, Q21, Q22, Q23, Q24, Q25, Q26, Q27, Q28, Q29, Q30, Q31, Q32, Q33, Q34, Q35, Q36, Q37, Q38, Q39, Q40, Q41, Q42, Q43, Q44, Q45, Q46, Q47, Q48, Q49, Q50, Q51, Q52, Q53, Q54, Q55, Q56, Q57, Q58, Q59, Q60, Q61, Q62]), "width" : 1 * mm, "tangentPropagation" : true});
        }
        {
            var Q0;
            Q0=makeQuery(id+"F6.boolean.opBoolean","INTERSECT",EDGE,{"derivedFrom":[makeQuery(id+"F5.opExtrude","SWEPT_FACE",FACE,{"disambiguationData":[OSD([sQuery(id+"F4.wireOp",EDGE,"E17")])]}),makeQuery(id+"F6.opExtrude","SWEPT_FACE",FACE,{"disambiguationData":[OSD([sQuery(id+"F0.wireOp",EDGE,"E9")])]})]});
            var Q1;
            Q1=makeQuery(id+"F6.boolean.opBoolean","INTERSECT",EDGE,{"derivedFrom":[makeQuery(id+"F3.opExtrude","SWEPT_FACE",FACE,{"disambiguationData":[OSD([sQuery(id+"F2.wireOp",EDGE,"E13")])]}),makeQuery(id+"F6.opExtrude","SWEPT_FACE",FACE,{"disambiguationData":[OSD([sQuery(id+"F0.wireOp",EDGE,"E10")])]})]});
            var Q2;
            Q2=makeQuery(id+"F1.opExtrude","CAP_EDGE",EDGE,{"disambiguationData":[OSD([sQuery(id+"F0.wireOp",EDGE,"E2")])],"isStart":true});
            var Q3;
            Q3=makeQuery(id+"F1.opExtrude","CAP_EDGE",EDGE,{"disambiguationData":[OSD([sQuery(id+"F0.wireOp",EDGE,"E5")])],"isStart":true});
            var Q4;
            Q4=makeQuery(id+"F1.opExtrude","CAP_EDGE",EDGE,{"disambiguationData":[OSD([sQuery(id+"F0.wireOp",EDGE,"E4")])],"isStart":true});
            var Q5;
            Q5=makeQuery(id+"F1.opExtrude","CAP_EDGE",EDGE,{"disambiguationData":[OSD([sQuery(id+"F0.wireOp",EDGE,"E1")])],"isStart":true});
            var Q6;
            Q6=makeQuery(id+"F1.opExtrude","CAP_EDGE",EDGE,{"disambiguationData":[OSD([sQuery(id+"F0.wireOp",EDGE,"E3")])],"isStart":true});
            var Q7;
            Q7=makeQuery(id+"F1.opExtrude","CAP_EDGE",EDGE,{"disambiguationData":[OSD([sQuery(id+"F0.wireOp",EDGE,"E6.trimOffspring")])],"isStart":true});
            chamfer(context, id + "F12", {"entities" : qUnion([Q0, Q1, Q2, Q3, Q4, Q5, Q6, Q7]), "width" : 0.5 * mm, "tangentPropagation" : true});
        }
        {
            var Q0;
            Q0=makeQuery(id+"F6.boolean.opBoolean","COPY",EDGE,{"derivedFrom":makeQuery(id+"F6.opExtrude","TWEAK_EDGE",EDGE,{"derivedFrom":[makeQuery(id+"F0.imprint","IMPRINT",EDGE,{"derivedFrom":sQuery(id+"F0.wireOp",EDGE,"E10")}),makeQuery(id+"F5.opExtrude","SWEPT_FACE",FACE,{"disambiguationData":[OSD([sQuery(id+"F4.wireOp",EDGE,"E15")])]})]})});
            var Q1;
            Q1=makeQuery(id+"F1.opExtrude","CAP_EDGE",EDGE,{"disambiguationData":[OSD([sQuery(id+"F0.wireOp",EDGE,"E1")])],"isStart":false});
            var Q2;
            Q2=makeQuery(id+"F1.opExtrude","CAP_EDGE",EDGE,{"disambiguationData":[OSD([sQuery(id+"F0.wireOp",EDGE,"E2")])],"isStart":false});
            var Q3;
            Q3=makeQuery(id+"F1.opExtrude","CAP_EDGE",EDGE,{"disambiguationData":[OSD([sQuery(id+"F0.wireOp",EDGE,"E5")])],"isStart":false});
            var Q4;
            Q4=makeQuery(id+"F1.opExtrude","CAP_EDGE",EDGE,{"disambiguationData":[OSD([sQuery(id+"F0.wireOp",EDGE,"E4")])],"isStart":false});
            var Q5;
            Q5=makeQuery(id+"F1.opExtrude","CAP_EDGE",EDGE,{"disambiguationData":[OSD([sQuery(id+"F0.wireOp",EDGE,"E3")])],"isStart":false});
            var Q6;
            Q6=makeQuery(id+"F1.opExtrude","CAP_EDGE",EDGE,{"disambiguationData":[OSD([sQuery(id+"F0.wireOp",EDGE,"E6.trimOffspring")])],"isStart":false});
            var Q7;
            Q7=makeQuery(id+"F6.boolean.opBoolean","COPY",EDGE,{"derivedFrom":makeQuery(id+"F6.opExtrude","TWEAK_EDGE",EDGE,{"derivedFrom":[makeQuery(id+"F0.imprint","IMPRINT",EDGE,{"derivedFrom":sQuery(id+"F0.wireOp",EDGE,"E9")}),makeQuery(id+"F5.opExtrude","SWEPT_FACE",FACE,{"disambiguationData":[OSD([sQuery(id+"F4.wireOp",EDGE,"E15")])]})]})});
            chamfer(context, id + "F13", {"entities" : qUnion([Q0, Q1, Q2, Q3, Q4, Q5, Q6, Q7]), "width" : 0.5 * mm, "tangentPropagation" : true});
        }
        {
            var Q0;
            {var subQ0=sQuery(id+"F0.wireOp",EDGE,"E2");var subQ1=sQuery(id+"F0.wireOp",EDGE,"E1");Q0=makeQuery(id+"F3.boolean.opBoolean","SPLIT",EDGE,{"disambiguationData":[TD([makeQuery(id+"F3.opExtrude","SWEPT_FACE",FACE,{"disambiguationData":[OSD([sQuery(id+"F2.wireOp",EDGE,"E13")])]})])],"derivedFrom":makeQuery(id+"F1.opExtrude","SWEPT_EDGE",EDGE,{"disambiguationData":[OSD([subQ1,subQ0])]})});}
            var Q1;
            {var subQ0=sQuery(id+"F0.wireOp",EDGE,"E4");var subQ1=sQuery(id+"F0.wireOp",EDGE,"E1");Q1=makeQuery(id+"F3.boolean.opBoolean","SPLIT",EDGE,{"disambiguationData":[TD([makeQuery(id+"F3.opExtrude","SWEPT_FACE",FACE,{"disambiguationData":[OSD([sQuery(id+"F2.wireOp",EDGE,"E13")])]})])],"derivedFrom":makeQuery(id+"F1.opExtrude","SWEPT_EDGE",EDGE,{"disambiguationData":[OSD([subQ1,subQ0])]})});}
            var Q2;
            {var subQ0=sQuery(id+"F0.wireOp",EDGE,"E6.trimOffspring");var subQ1=sQuery(id+"F0.wireOp",EDGE,"E3");Q2=makeQuery(id+"F5.boolean.opBoolean","SPLIT",EDGE,{"disambiguationData":[TD([makeQuery(id+"F5.opExtrude","SWEPT_FACE",FACE,{"disambiguationData":[OSD([sQuery(id+"F4.wireOp",EDGE,"E17")])]})])],"derivedFrom":makeQuery(id+"F1.opExtrude","SWEPT_EDGE",EDGE,{"disambiguationData":[OSD([subQ1,subQ0])]})});}
            var Q3;
            {var subQ0=sQuery(id+"F0.wireOp",EDGE,"E4");var subQ1=sQuery(id+"F0.wireOp",EDGE,"E3");Q3=makeQuery(id+"F5.boolean.opBoolean","SPLIT",EDGE,{"disambiguationData":[TD([makeQuery(id+"F5.opExtrude","SWEPT_FACE",FACE,{"disambiguationData":[OSD([sQuery(id+"F4.wireOp",EDGE,"E17")])]})])],"derivedFrom":makeQuery(id+"F1.opExtrude","SWEPT_EDGE",EDGE,{"disambiguationData":[OSD([subQ1,subQ0])]})});}
            var Q4;
            {var subQ0=sQuery(id+"F0.wireOp",EDGE,"E3");var subQ1=sQuery(id+"F0.wireOp",EDGE,"E6.trimOffspring");Q4=makeQuery(id+"F5.boolean.opBoolean","SPLIT",EDGE,{"disambiguationData":[TD([makeQuery(id+"F5.opExtrude","SWEPT_FACE",FACE,{"disambiguationData":[OSD([sQuery(id+"F4.wireOp",EDGE,"E15")])]})])],"derivedFrom":makeQuery(id+"F1.opExtrude","SWEPT_EDGE",EDGE,{"disambiguationData":[OSD([subQ0,subQ1])]})});}
            var Q5;
            {var subQ0=sQuery(id+"F0.wireOp",EDGE,"E4");var subQ1=sQuery(id+"F0.wireOp",EDGE,"E3");Q5=makeQuery(id+"F5.boolean.opBoolean","SPLIT",EDGE,{"disambiguationData":[TD([makeQuery(id+"F5.opExtrude","SWEPT_FACE",FACE,{"disambiguationData":[OSD([sQuery(id+"F4.wireOp",EDGE,"E15")])]})])],"derivedFrom":makeQuery(id+"F1.opExtrude","SWEPT_EDGE",EDGE,{"disambiguationData":[OSD([subQ1,subQ0])]})});}
            var Q6;
            {var subQ0=sQuery(id+"F0.wireOp",EDGE,"E2");var subQ1=sQuery(id+"F0.wireOp",EDGE,"E1");Q6=makeQuery(id+"F3.boolean.opBoolean","SPLIT",EDGE,{"disambiguationData":[TD([makeQuery(id+"F3.opExtrude","SWEPT_FACE",FACE,{"disambiguationData":[OSD([sQuery(id+"F2.wireOp",EDGE,"E11")])]})])],"derivedFrom":makeQuery(id+"F1.opExtrude","SWEPT_EDGE",EDGE,{"disambiguationData":[OSD([subQ1,subQ0])]})});}
            var Q7;
            {var subQ0=sQuery(id+"F0.wireOp",EDGE,"E4");var subQ1=sQuery(id+"F0.wireOp",EDGE,"E1");Q7=makeQuery(id+"F3.boolean.opBoolean","SPLIT",EDGE,{"disambiguationData":[TD([makeQuery(id+"F3.opExtrude","SWEPT_FACE",FACE,{"disambiguationData":[OSD([sQuery(id+"F2.wireOp",EDGE,"E11")])]})])],"derivedFrom":makeQuery(id+"F1.opExtrude","SWEPT_EDGE",EDGE,{"disambiguationData":[OSD([subQ1,subQ0])]})});}
            chamfer(context, id + "F14", {"entities" : qUnion([Q0, Q1, Q2, Q3, Q4, Q5, Q6, Q7]), "width" : 0.5 * mm, "tangentPropagation" : true});
        }
    });
